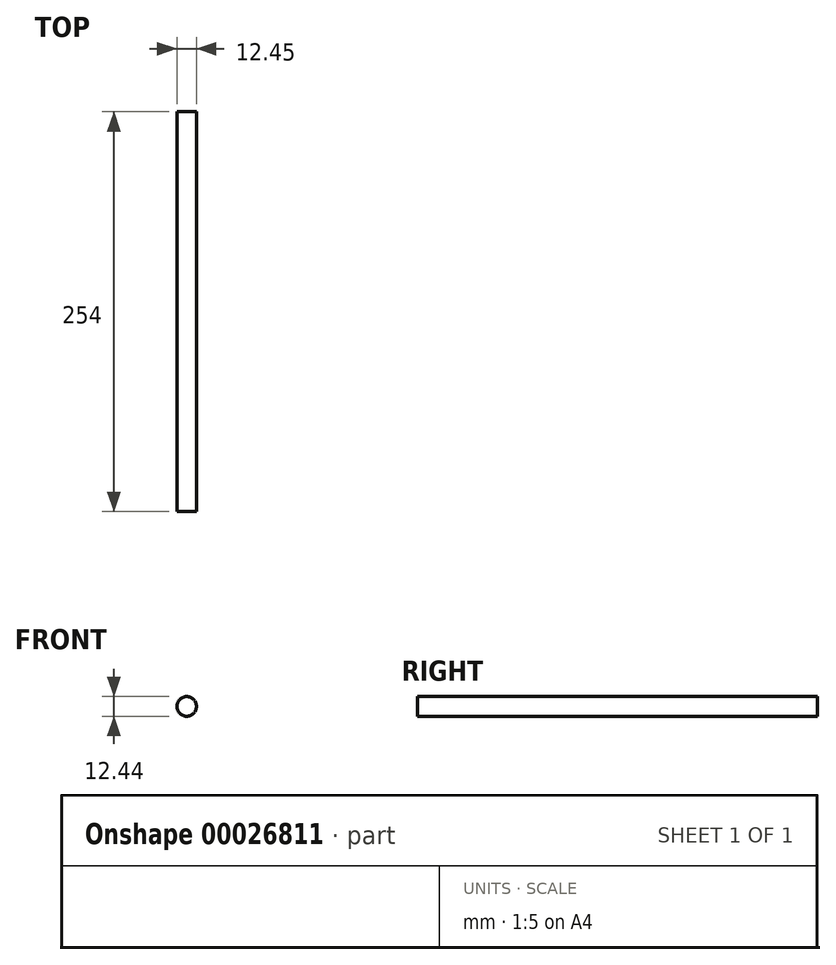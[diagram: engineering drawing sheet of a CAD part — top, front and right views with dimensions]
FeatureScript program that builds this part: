
annotation { "Feature Type Name" : "Feature", "Feature Type Description" : "" }
export const myFeature = defineFeature(function(context is Context, id is Id, definition is map)
    precondition{}
    {
        {
            var Q0;
            Q0=qCreatedBy(makeId("Front.planeOp"),FACE);
            var sketch = newSketch(context, id + "F0", { "sketchPlane" : qUnion([Q0])});
            skCircle(sketch, "E0", {"center": v(-14.3, -4.62) * mm, "radius": 6.22 * mm});
            skSolve(sketch);
        }
        {
            var Q0;
            Q0=makeQuery(id+"F0.imprint","IMPRINT",FACE,{"disambiguationData":[TD([[makeQuery(id+"F0.imprint","IMPRINT",EDGE,{"derivedFrom":sQuery(id+"F0.wireOp",EDGE,"E0")}),1.0]])]});
            extrude(context, id + "F1", {"entities" : qUnion([Q0]), "depth" : 254 * mm});
        }
    });
